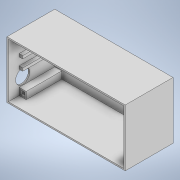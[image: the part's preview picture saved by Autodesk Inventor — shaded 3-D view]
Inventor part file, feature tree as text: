
AUTODESK INVENTOR PART (.ipt)
format: ipt  version: 2022 (Build 260153000, 153)  size: 211,456 bytes
history: native  units: mm
features: sketch x6, extrude x5, hole x1
ambient origin geometry x8: Origin, YZ Plane, XZ Plane, XY Plane, X Axis, Y Axis, Z Axis, Center Point
bodies: Volumenkörper1 (feature_tree)
feature tree (12):
  extrude  "Extrusion1"  Depth=166.0mm
  extrude  "Extrusion2"  Depth=2.0mm
  extrude  "Extrusion3"  Depth=2.0mm
  extrude  "Extrusion4"  Depth=65.0mm TaperAngle=0.0deg
  hole  "Bohrung1"  [1 undecoded]
  extrude  "Extrusion5"  Depth=10.0mm
  sketch  "Skizze1"  dims[d0=80.0mm d1=166.0mm]
  sketch  "Skizze2"  dims[d2=2.0mm d3=0.0mm d4=2.0mm]
  sketch  "Skizze3"  dims[d6=2.0mm d7=2.0mm]
  sketch  "Skizze4"  dims[d8=2.0mm d9=65.0mm d10=0.0mm]
  sketch  "Skizze5"  dims[d13=20.0mm d14=6.0mm d15=4.0mm d16=2.0mm d17=90.0deg d18=8.0mm d19=20.594885mm d20=10.0mm]
  sketch  "Skizze6"  dims[d21=10.0mm d22=10.0mm d23=10.0mm d24=50.0mm d25=0.0mm d30=11.0mm d31=4.0mm d32=4.0mm d33=5.0mm d34=25.0mm d37=5.0mm d38=0.0mm d39=50.0mm d40=0.0mm d41=10.0mm d42=5.7mm d43=6.3mm d44=2.15mm d45=1.85mm d46=6.3mm d47=1.85mm d48=5.7mm d49=2.15mm d50=3.0mm d51=0.0mm d52=11.0mm d53=11.0mm d54=45.0mm d55=10.0mm d56=1.85mm d57=6.3mm d58=25.0mm d59=4.0mm d60=11.0mm]
note: 1 required parameter value undecoded (feature->parameter linkage not recoverable at this tier; creation-order binding heuristic only, values carry confidence <= 0.55)
